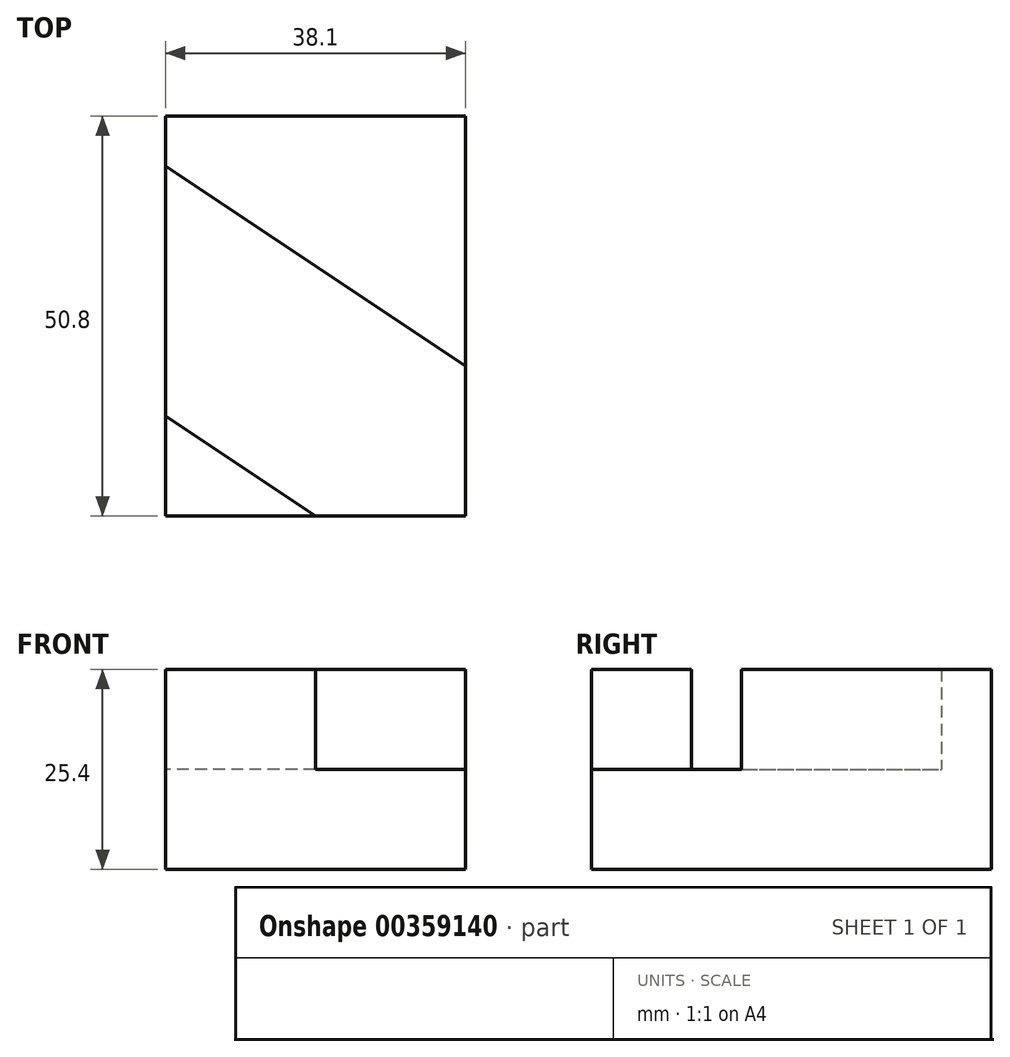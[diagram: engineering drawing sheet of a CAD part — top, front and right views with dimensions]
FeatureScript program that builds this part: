
annotation { "Feature Type Name" : "Feature", "Feature Type Description" : "" }
export const myFeature = defineFeature(function(context is Context, id is Id, definition is map)
    precondition{}
    {
        {
            var Q0;
            Q0=qCreatedBy(makeId("Front.planeOp"),FACE);
            var sketch = newSketch(context, id + "F0", { "sketchPlane" : qUnion([Q0])});
            skLineSegment(sketch, "E0", {"start": v(-21.68, 27.87) * mm, "end": v(16.42, 27.87) * mm});
            skLineSegment(sketch, "E1", {"start": v(16.42, 27.87) * mm, "end": v(16.42, 15.17) * mm});
            skLineSegment(sketch, "E2", {"start": v(16.42, 15.17) * mm, "end": v(-21.68, 15.17) * mm});
            skLineSegment(sketch, "E3", {"start": v(-21.68, 15.17) * mm, "end": v(-21.68, 27.87) * mm});
            skSolve(sketch);
        }
        {
            var Q0;
            Q0 = qSketchRegion(id + "F0", true);
            extrude(context, id + "F1", {"entities" : qUnion([Q0]), "depth" : 50.8 * mm});
        }
        {
            var Q0;
            Q0=makeQuery(id+"F1.opExtrude","SWEPT_FACE",FACE,{"disambiguationData":[OSD([sQuery(id+"F0.wireOp",EDGE,"E0")])]});
            var sketch = newSketch(context, id + "F2", { "sketchPlane" : qUnion([Q0])});
            skLineSegment(sketch, "E4", {"start": v(-21.68, -50.8) * mm, "end": v(-2.63, -50.8) * mm});
            skLineSegment(sketch, "E5", {"start": v(-2.63, -50.8) * mm, "end": v(-21.68, -38.1) * mm});
            skLineSegment(sketch, "E6", {"start": v(-21.68, -38.1) * mm, "end": v(-21.68, -50.8) * mm});
            skSolve(sketch);
        }
        {
            var Q0;
            Q0 = qSketchRegion(id + "F2", true);
            extrude(context, id + "F3", {"entities" : qUnion([Q0]), "operationType" : NewBodyOperationType.ADD, "depth" : 12.7 * mm});
        }
        {
            var Q0;
            Q0=makeQuery(id+"F1.opExtrude","SWEPT_FACE",FACE,{"disambiguationData":[OSD([sQuery(id+"F0.wireOp",EDGE,"E0")])]});
            var sketch = newSketch(context, id + "F4", { "sketchPlane" : qUnion([Q0])});
            skLineSegment(sketch, "E7", {"start": v(16.42, 0) * mm, "end": v(16.42, -31.75) * mm});
            skLineSegment(sketch, "E8", {"start": v(16.42, -31.75) * mm, "end": v(-21.68, -6.35) * mm});
            skLineSegment(sketch, "E9", {"start": v(-21.68, -6.35) * mm, "end": v(-21.68, 0) * mm});
            skLineSegment(sketch, "E10", {"start": v(-21.68, 0) * mm, "end": v(16.42, 0) * mm});
            skSolve(sketch);
        }
        {
            var Q0;
            Q0 = qSketchRegion(id + "F4", true);
            extrude(context, id + "F5", {"entities" : qUnion([Q0]), "operationType" : NewBodyOperationType.ADD, "depth" : 12.7 * mm});
        }
    });
